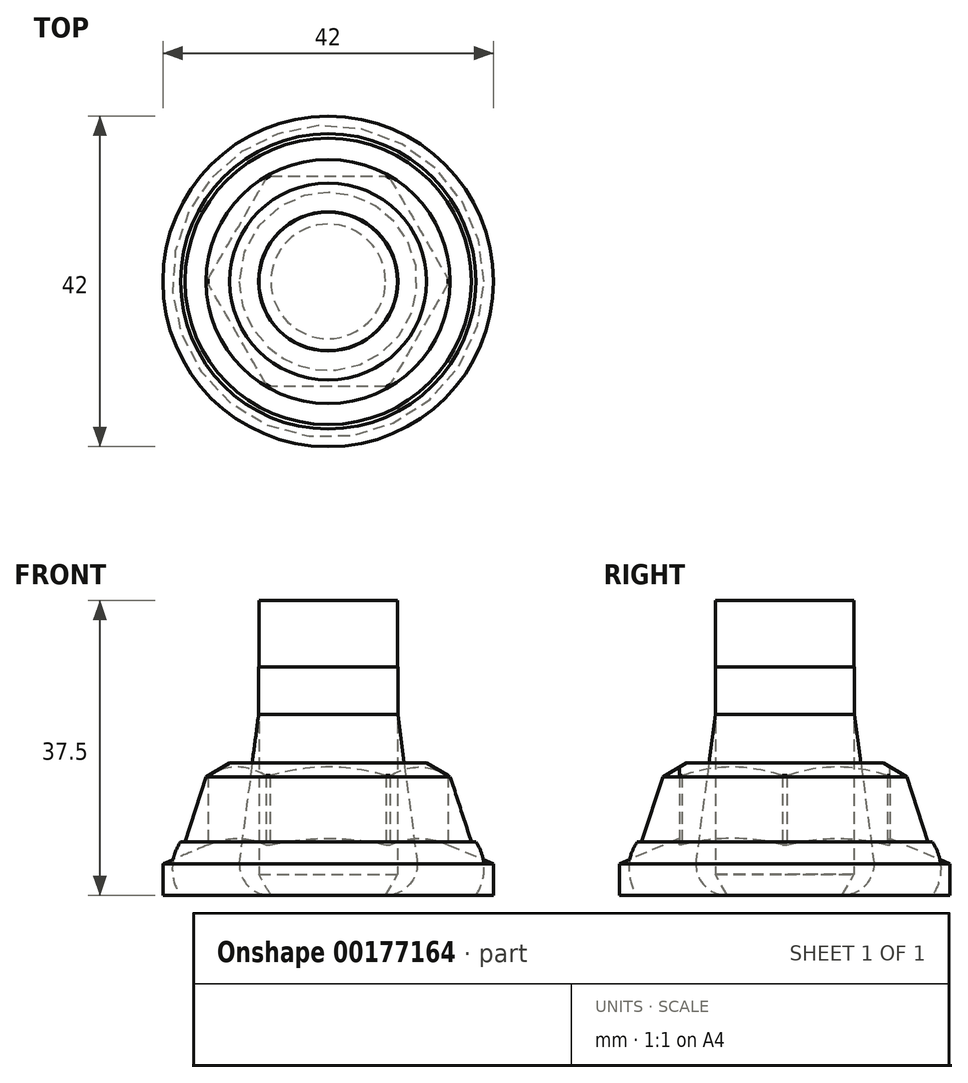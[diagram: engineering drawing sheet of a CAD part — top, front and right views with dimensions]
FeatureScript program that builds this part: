
annotation { "Feature Type Name" : "Feature", "Feature Type Description" : "" }
export const myFeature = defineFeature(function(context is Context, id is Id, definition is map)
    precondition{}
    {
        {
            var Q0;
            Q0=qCreatedBy(makeId("Front.planeOp"),FACE);
            var sketch = newSketch(context, id + "F0", { "sketchPlane" : qUnion([Q0]), "disableImprinting" : false});
            skLineSegment(sketch, "E0", {"start": v(0, 0) * mm, "end": v(0, 16.8) * mm});
            skLineSegment(sketch, "E1", {"start": v(0, 16.8) * mm, "end": v(12.5, 16.8) * mm});
            skLineSegment(sketch, "E2", {"start": v(15.25, 15.21) * mm, "end": v(15.25, 6.44) * mm});
            skLineSegment(sketch, "E3", {"start": v(15.25, 6.44) * mm, "end": v(21, 4) * mm});
            skLineSegment(sketch, "E4", {"start": v(21, 4) * mm, "end": v(21, 0) * mm});
            skLineSegment(sketch, "E5", {"start": v(21, 0) * mm, "end": v(0, 0) * mm});
            skLineSegment(sketch, "E6", {"start": v(12.5, 16.8) * mm, "end": v(15.25, 15.21) * mm});
            skLineSegment(sketch, "E7", {"start": v(0, 0) * mm, "end": v(0, 16.8) * mm, "construction": true});
            skSolve(sketch);
        }
        {
            var Q0;
            Q0=qSketchRegion(id+"F0",true);
            var Q1;
            Q1=sQuery(id+"F0.wireOp",EDGE,"E0");
            revolve(context, id + "F1", {"entities" : qUnion([Q0]), "axis" : qUnion([Q1]), "revolveType" : RevolveType.FULL});
        }
        {
            var Q0;
            Q0=makeQuery(id+"F1.opRevolve","SWEPT_FACE",FACE,{"disambiguationData":[OSD([sQuery(id+"F0.wireOp",EDGE,"E1")])]});
            var sketch = newSketch(context, id + "F2", { "sketchPlane" : qUnion([Q0])});
            skCircle(sketch, "E8.cCircle", {"center": v(0, 0) * mm, "radius": 13.35 * mm, "construction": true});
            skLineSegment(sketch, "E8.0", {"start": v(-7.7, 13.35) * mm, "end": v(7.7, 13.35) * mm});
            skLineSegment(sketch, "E8.1", {"start": v(7.7, 13.35) * mm, "end": v(15.42, 0) * mm});
            skLineSegment(sketch, "E8.2", {"start": v(15.42, 0) * mm, "end": v(7.7, -13.35) * mm});
            skLineSegment(sketch, "E8.3", {"start": v(7.7, -13.35) * mm, "end": v(-7.7, -13.35) * mm});
            skLineSegment(sketch, "E8.4", {"start": v(-7.7, -13.35) * mm, "end": v(-15.42, 0) * mm});
            skLineSegment(sketch, "E8.5", {"start": v(-15.42, 0) * mm, "end": v(-7.7, 13.35) * mm});
            skPoint(sketch, "E8.0.midPoint", {"position": v(0, 13.35) * mm});
            skCircle(sketch, "E9", {"center": v(0, 0) * mm, "radius": 25.92 * mm});
            skSolve(sketch);
        }
        {
            var Q0;
            Q0=qSketchRegion(id+"F2",true);
            var Q1;
            Q1=makeQuery(id+"F1.opRevolve","SWEPT_FACE",FACE,{"disambiguationData":[OSD([sQuery(id+"F0.wireOp",EDGE,"E3")])]});
            extrude(context, id + "F3", {"entities" : qUnion([Q0]), "operationType" : NewBodyOperationType.REMOVE, "endBound" : BoundingType.UP_TO_SURFACE, "oppositeDirection" : true, "endBoundEntityFace" : qUnion([Q1]), "depth" : 25 * mm, "offsetDistance" : 25 * mm});
        }
        {
            var Q0;
            Q0=qCreatedBy(makeId("Front.planeOp"),FACE);
            var sketch = newSketch(context, id + "F4", { "sketchPlane" : qUnion([Q0])});
            skLineSegment(sketch, "E10", {"start": v(0, 0) * mm, "end": v(0, 29) * mm});
            skLineSegment(sketch, "E11", {"start": v(0, 29) * mm, "end": v(8.84, 29) * mm});
            skLineSegment(sketch, "E12", {"start": v(8.84, 29) * mm, "end": v(8.84, 23) * mm});
            skLineSegment(sketch, "E13", {"start": v(8.84, 23) * mm, "end": v(11.27, 4.52) * mm});
            skLineSegment(sketch, "E14", {"start": v(7.3, 0) * mm, "end": v(0, 0) * mm});
            skLineSegment(sketch, "E15", {"start": v(0, 0) * mm, "end": v(0, 29) * mm, "construction": true});
            skPoint(sketch, "E16.visualSharp", {"position": v(11.87, 0) * mm});
            skArc(sketch, "E16.filletArc", {"start": v(7.3, 0) * mm, "mid": v(10.31, 1.36) * mm, "end": v(11.27, 4.52) * mm});
            skSolve(sketch);
        }
        {
            var Q0;
            Q0=makeQuery(id+"F4.imprint","IMPRINT",FACE,{"disambiguationData":[TD([[makeQuery(id+"F4.imprint","IMPRINT",EDGE,{"derivedFrom":sQuery(id+"F4.wireOp",EDGE,"E10")}),-1.0]])]});
            var Q1;
            Q1=sQuery(id+"F4.wireOp",EDGE,"E10");
            revolve(context, id + "F5", {"surfaceOperationType" : NewSurfaceOperationType.NEW, "entities" : qUnion([Q0]), "axis" : qUnion([Q1]), "revolveType" : RevolveType.FULL});
        }
        {
            var Q0;
            Q0=qCreatedBy(makeId("Front.planeOp"),FACE);
            var sketch = newSketch(context, id + "F6", { "sketchPlane" : qUnion([Q0])});
            skLineSegment(sketch, "E17", {"start": v(0, 0) * mm, "end": v(0, 16.8) * mm, "construction": true});
            skLineSegment(sketch, "E18", {"start": v(0, 16.8) * mm, "end": v(12.5, 16.8) * mm});
            skLineSegment(sketch, "E19", {"start": v(12.5, 16.8) * mm, "end": v(15.5, 15.07) * mm});
            skLineSegment(sketch, "E20", {"start": v(15.5, 15.07) * mm, "end": v(18.19, 6.8) * mm});
            skLineSegment(sketch, "E21", {"start": v(18.75, 0) * mm, "end": v(0, 0) * mm});
            skLineSegment(sketch, "E22", {"start": v(0, 16.8) * mm, "end": v(0, 0) * mm});
            skLineSegment(sketch, "E23", {"start": v(18.19, 6.8) * mm, "end": v(18.75, 6.8) * mm});
            skArc(sketch, "E24", {"start": v(18.75, 0) * mm, "mid": v(19.8, 3.4) * mm, "end": v(18.75, 6.8) * mm});
            skSolve(sketch);
        }
        {
            var Q0;
            Q0=qSketchRegion(id+"F6",true);
            var Q1;
            Q1=sQuery(id+"F6.wireOp",EDGE,"E22");
            revolve(context, id + "F7", {"surfaceOperationType" : NewSurfaceOperationType.NEW, "entities" : qUnion([Q0]), "axis" : qUnion([Q1]), "revolveType" : RevolveType.FULL});
        }
        {
            var Q0;
            Q0=qCreatedBy(makeId("Front.planeOp"),FACE);
            var sketch = newSketch(context, id + "F8", { "sketchPlane" : qUnion([Q0])});
            skLineSegment(sketch, "E25", {"start": v(0, 0) * mm, "end": v(0, 37.5) * mm});
            skLineSegment(sketch, "E26", {"start": v(0, 37.5) * mm, "end": v(8.8, 37.5) * mm});
            skLineSegment(sketch, "E27", {"start": v(8.8, 37.5) * mm, "end": v(8.8, 2.64) * mm});
            skLineSegment(sketch, "E28", {"start": v(8.8, 2.64) * mm, "end": v(7.28, 0) * mm});
            skLineSegment(sketch, "E29", {"start": v(7.28, 0) * mm, "end": v(0, 0) * mm});
            skLineSegment(sketch, "E30", {"start": v(0, 37.5) * mm, "end": v(0, 0) * mm, "construction": true});
            skSolve(sketch);
        }
        {
            var Q0;
            Q0=qSketchRegion(id+"F8",true);
            var Q1;
            Q1=sQuery(id+"F8.wireOp",EDGE,"E25");
            revolve(context, id + "F9", {"surfaceOperationType" : NewSurfaceOperationType.NEW, "entities" : qUnion([Q0]), "axis" : qUnion([Q1]), "revolveType" : RevolveType.FULL});
        }
    });
